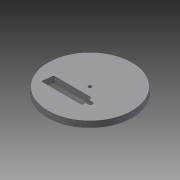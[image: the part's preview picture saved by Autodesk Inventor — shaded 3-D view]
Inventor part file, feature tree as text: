
AUTODESK INVENTOR PART (.ipt)
format: ipt  version: 2015 (Build 190159000, 159)  size: 119,296 bytes
history: native  units: mm
features: extrude x3, chamfer x2, fillet x2, sketch x2
ambient origin geometry x8: Origin, YZ Plane, XZ Plane, XY Plane, X Axis, Y Axis, Z Axis, Center Point
bodies: Solid1 (feature_tree)
feature tree (9):
  extrude  "Extrusion1"  Depth=85.75mm
  extrude  "Extrusion2"  Depth=2.0mm
  chamfer  "Chamfer1"  Distance=11.0mm
  chamfer  "Chamfer2"  Distance=9.0mm
  fillet  "Fillet1"  Radius=12.0mm
  extrude  "Extrusion3"  Depth=6.0mm TaperAngle=0.0deg
  fillet  "Fillet2"  Radius=11.0mm
  sketch  "Sketch1"  dims[d0=3.0mm d1=85.75mm]
  sketch  "Sketch2"  dims[d2=6.0mm d3=0.0mm d4=41.5mm d5=11.0mm d6=9.0mm d7=12.0mm d8=6.0mm d9=0.0mm d10=11.0mm d11=1.5mm d12=45.0deg d13=11.0mm d14=1.5mm d15=45.0deg d16=1.0mm d19=6.0mm d20=0.0mm d21=1.0mm d23=3.0mm d24=2.0mm]
